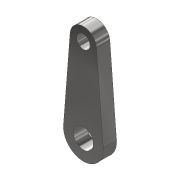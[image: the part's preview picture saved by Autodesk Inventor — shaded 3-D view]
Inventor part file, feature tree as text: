
AUTODESK INVENTOR PART (.ipt)
format: ipt  version: 2021 (Build 250183000, 183)  size: 95,232 bytes
history: native  units: mm
features: extrude x1, sketch x1
ambient origin geometry x8: Origin, YZ Plane, XZ Plane, XY Plane, X Axis, Y Axis, Z Axis, Center Point
bodies: Solid1 (feature_tree)
feature tree (2):
  extrude  "Extrusion1"  Depth=10.0mm
  sketch  "Sketch1"  dims[d0=63.0mm d1=30.0mm d2=20.0mm d3=10.0mm d4=15.0mm d5=10.0mm d6=0.0mm]
